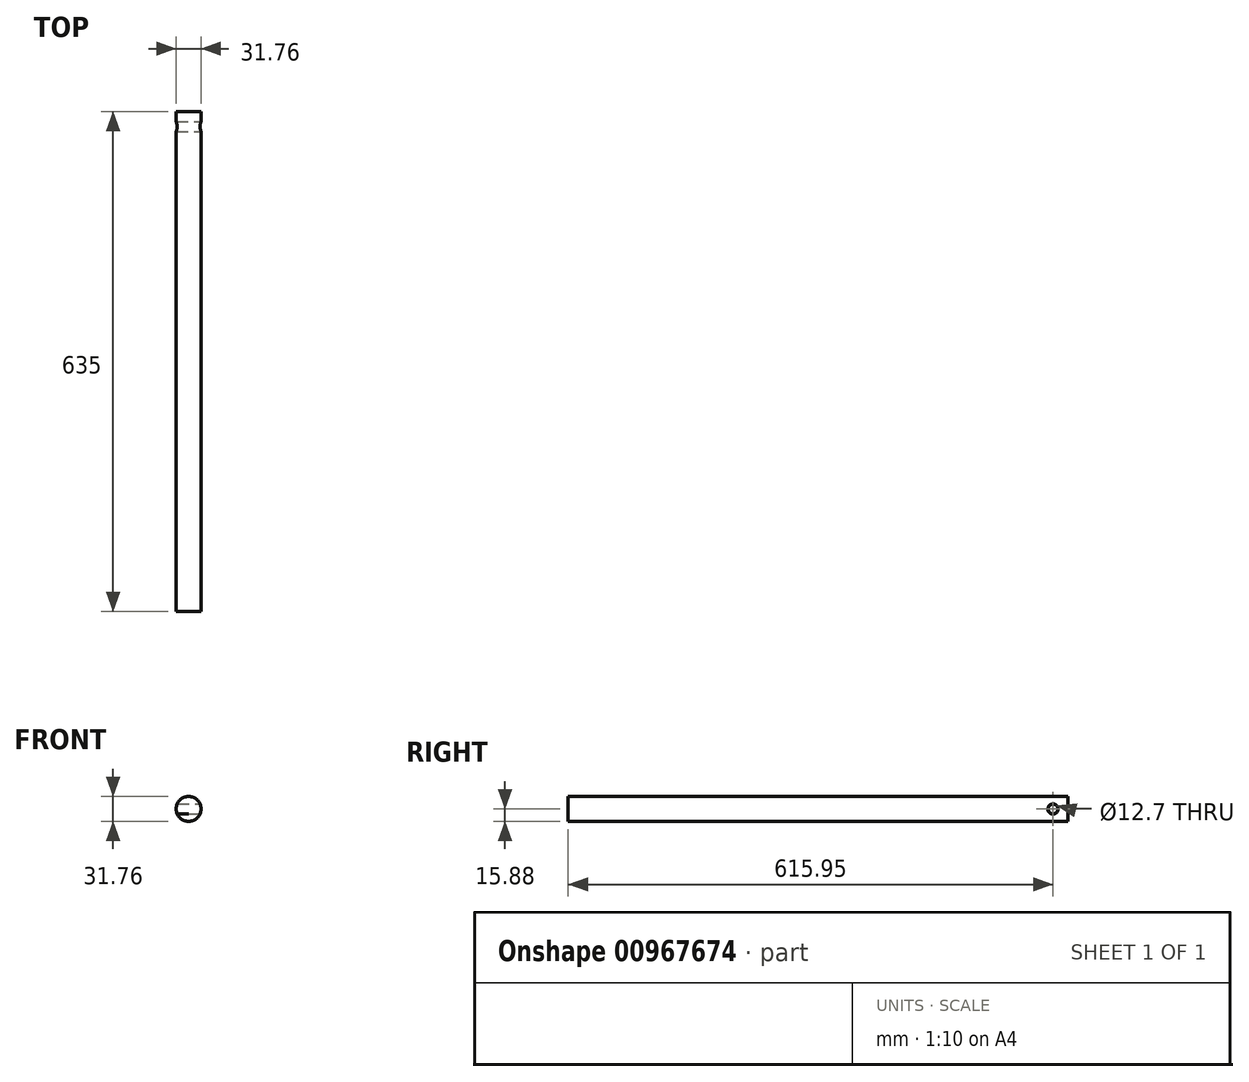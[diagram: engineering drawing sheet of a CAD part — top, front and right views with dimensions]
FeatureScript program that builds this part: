
annotation { "Feature Type Name" : "Feature", "Feature Type Description" : "" }
export const myFeature = defineFeature(function(context is Context, id is Id, definition is map)
    precondition{}
    {
        {
            var Q0;
            Q0=qCreatedBy(makeId("Front.planeOp"),FACE);
            var sketch = newSketch(context, id + "F0", { "sketchPlane" : qUnion([Q0])});
            skCircle(sketch, "E0", {"center": v(0, 0) * mm, "radius": 15.88 * mm});
            skSolve(sketch);
        }
        {
            var Q0;
            Q0 = qSketchRegion(id + "F0", true);
            extrude(context, id + "F1", {"entities" : qUnion([Q0]), "depth" : 635 * mm, "offsetDistance" : 25.4 * mm});
        }
        {
            var Q0;
            Q0=qCreatedBy(makeId("Right.planeOp"),FACE);
            var sketch = newSketch(context, id + "F2", { "sketchPlane" : qUnion([Q0])});
            skCircle(sketch, "E1", {"center": v(-19.05, 0) * mm, "radius": 6.35 * mm});
            skSolve(sketch);
        }
        {
            var Q0;
            Q0 = qSketchRegion(id + "F2", true);
            extrude(context, id + "F3", {"entities" : qUnion([Q0]), "operationType" : NewBodyOperationType.REMOVE, "endBound" : BoundingType.THROUGH_ALL, "oppositeDirection" : true, "depth" : 25.4 * mm, "offsetDistance" : 25.4 * mm, "hasSecondDirection" : true, "secondDirectionBound" : BoundingType.THROUGH_ALL, "secondDirectionOppositeDirection" : false, "secondDirectionDepth" : 25.4 * mm});
        }
    });
